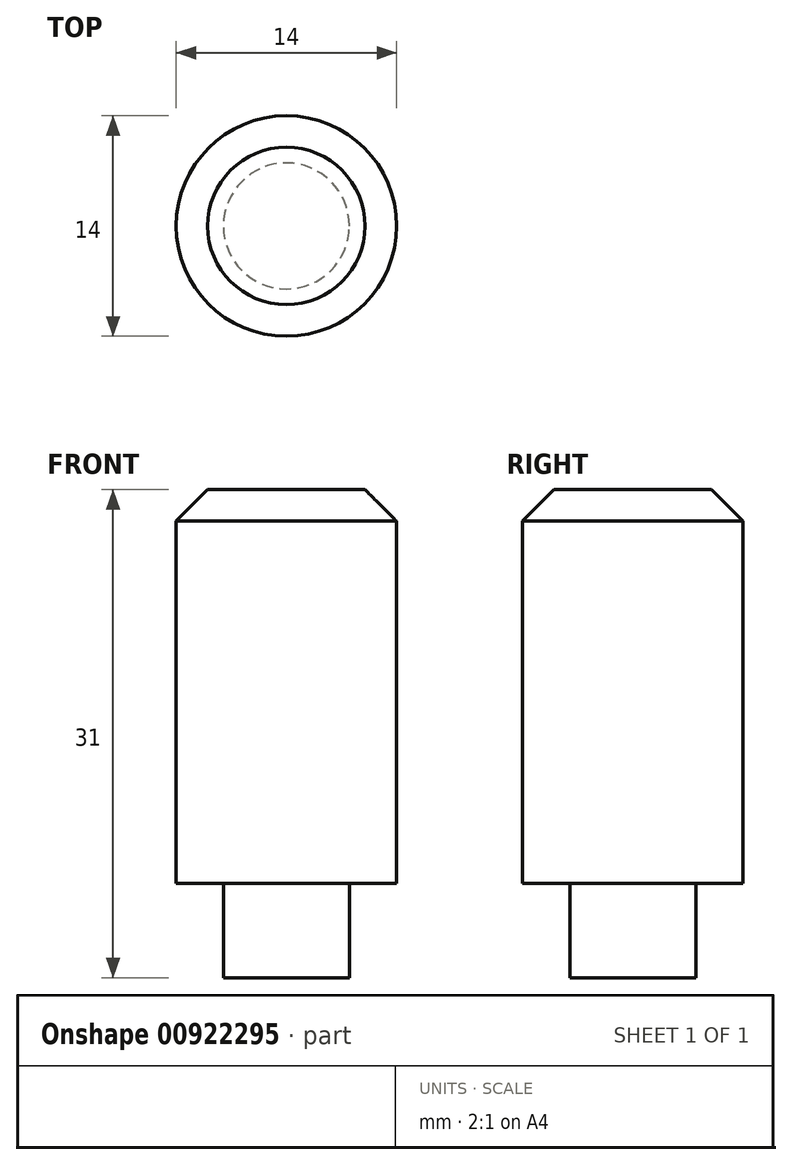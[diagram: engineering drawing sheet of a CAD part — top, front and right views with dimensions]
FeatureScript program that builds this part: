
annotation { "Feature Type Name" : "Feature", "Feature Type Description" : "" }
export const myFeature = defineFeature(function(context is Context, id is Id, definition is map)
    precondition{}
    {
        {
            var Q0;
            Q0=qCreatedBy(makeId("Top.planeOp"),FACE);
            var sketch = newSketch(context, id + "F0", { "sketchPlane" : qUnion([Q0])});
            skCircle(sketch, "E0", {"center": v(0, 0) * mm, "radius": 7 * mm});
            skSolve(sketch);
        }
        {
            var Q0;
            Q0=makeQuery(id+"F0.imprint","IMPRINT",FACE,{"disambiguationData":[TD([[makeQuery(id+"F0.imprint","IMPRINT",EDGE,{"derivedFrom":sQuery(id+"F0.wireOp",EDGE,"E0")}),1.0]])]});
            extrude(context, id + "F1", {"entities" : qUnion([Q0]), "endBound" : BoundingType.SYMMETRIC, "oppositeDirection" : true, "depth" : 25 * mm, "offsetDistance" : 25 * mm});
        }
        {
            var Q0;
            Q0=makeQuery(id+"F1.opExtrude","CAP_EDGE",EDGE,{"disambiguationData":[OSD([sQuery(id+"F0.wireOp",EDGE,"E0")])],"isStart":true});
            chamfer(context, id + "F2", {"entities" : qUnion([Q0]), "width" : 2 * mm, "tangentPropagation" : true});
        }
        {
            var Q0;
            Q0=makeQuery(id+"F1.opExtrude","CAP_FACE",FACE,{"disambiguationData":[OSD([sQuery(id+"F0.wireOp",EDGE,"E0")])],"isStart":false});
            var sketch = newSketch(context, id + "F3", { "sketchPlane" : qUnion([Q0])});
            skCircle(sketch, "E1", {"center": v(0, 0) * mm, "radius": 4 * mm});
            skSolve(sketch);
        }
        {
            var Q0;
            Q0 = qSketchRegion(id + "F3", true);
            extrude(context, id + "F4", {"entities" : qUnion([Q0]), "operationType" : NewBodyOperationType.ADD, "depth" : 6 * mm, "offsetDistance" : 25 * mm});
        }
    });
